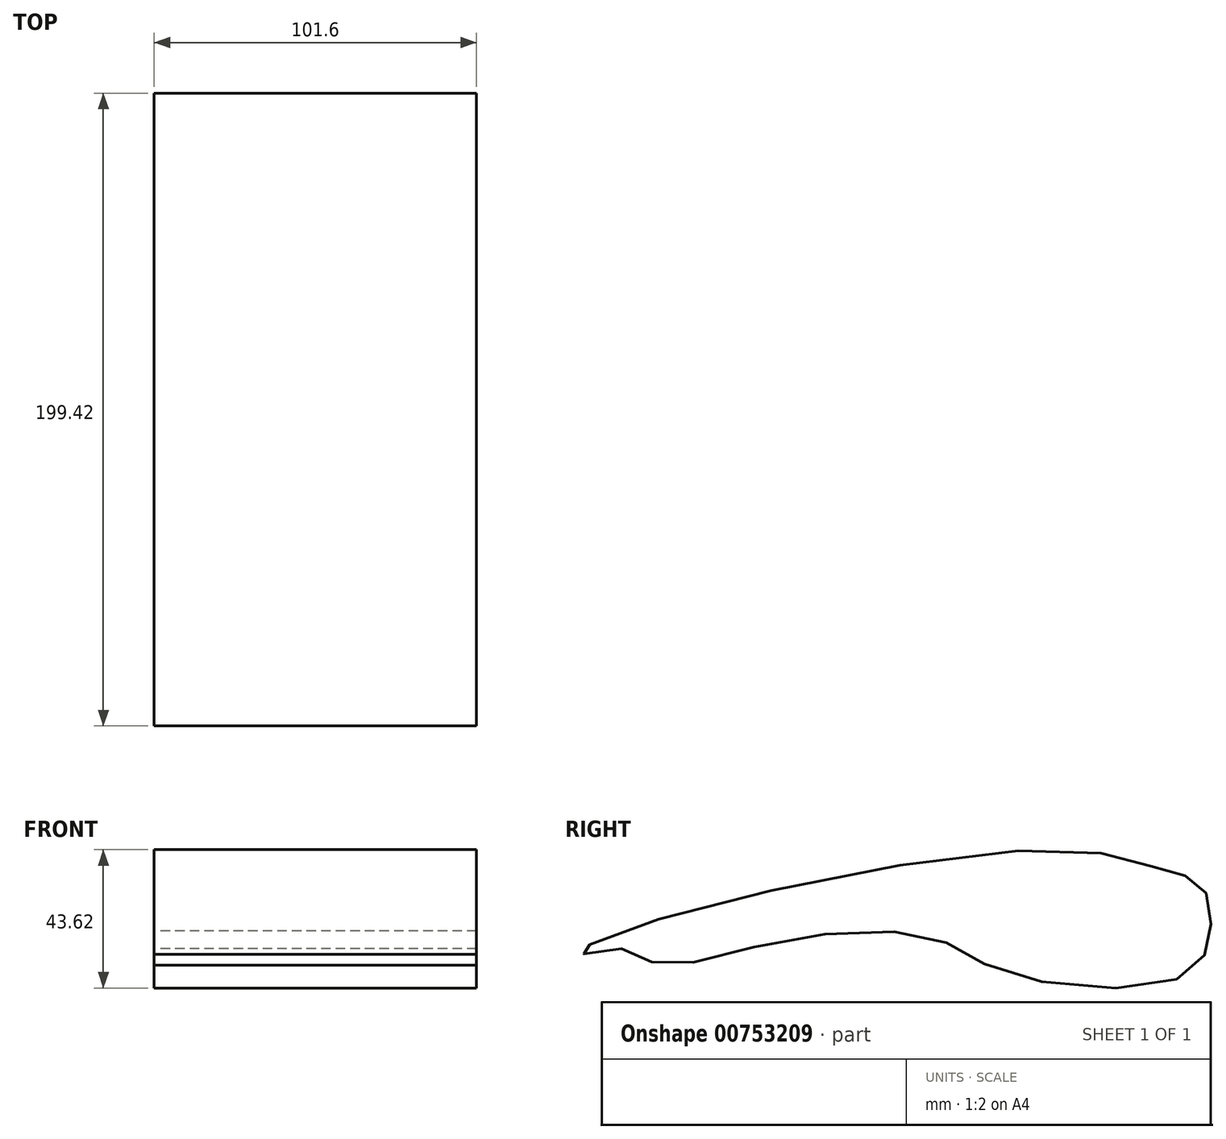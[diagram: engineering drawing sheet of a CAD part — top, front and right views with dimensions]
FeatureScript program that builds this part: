
annotation { "Feature Type Name" : "Feature", "Feature Type Description" : "" }
export const myFeature = defineFeature(function(context is Context, id is Id, definition is map)
    precondition{}
    {
        {
            var Q0;
            Q0=qCreatedBy(makeId("Right.planeOp"),FACE);
            var sketch = newSketch(context, id + "F0", { "sketchPlane" : qUnion([Q0])});
            skFitSpline(sketch, "E0", {"points": [v(-90.43, 0) * mm, v(-78.81, -4.89) * mm, v(-42.68, 1.94) * mm, v(7.84, 3.41) * mm, v(29.77, -7.28) * mm, v(82.68, -10.23) * mm, v(94.11, 0) * mm, v(95.03, 11.52) * mm, v(91.72, 20.74) * mm, v(81.02, 24.61) * mm, v(45.63, 31.25) * mm, v(-96.88, 3.04) * mm, v(-103.88, -1.75) * mm, v(-90.43, 0) * mm]});
            skSolve(sketch);
        }
        {
            var Q0;
            Q0 = qSketchRegion(id + "F0", true);
            extrude(context, id + "F1", {"entities" : qUnion([Q0]), "depth" : 50.8 * mm, "offsetDistance" : 25.4 * mm});
        }
        {
            var Q0;
            Q0 = qSketchRegion(id + "F0", true);
            extrude(context, id + "F2", {"entities" : qUnion([Q0]), "operationType" : NewBodyOperationType.ADD, "oppositeDirection" : true, "depth" : 50.8 * mm, "offsetDistance" : 25.4 * mm});
        }
    });
